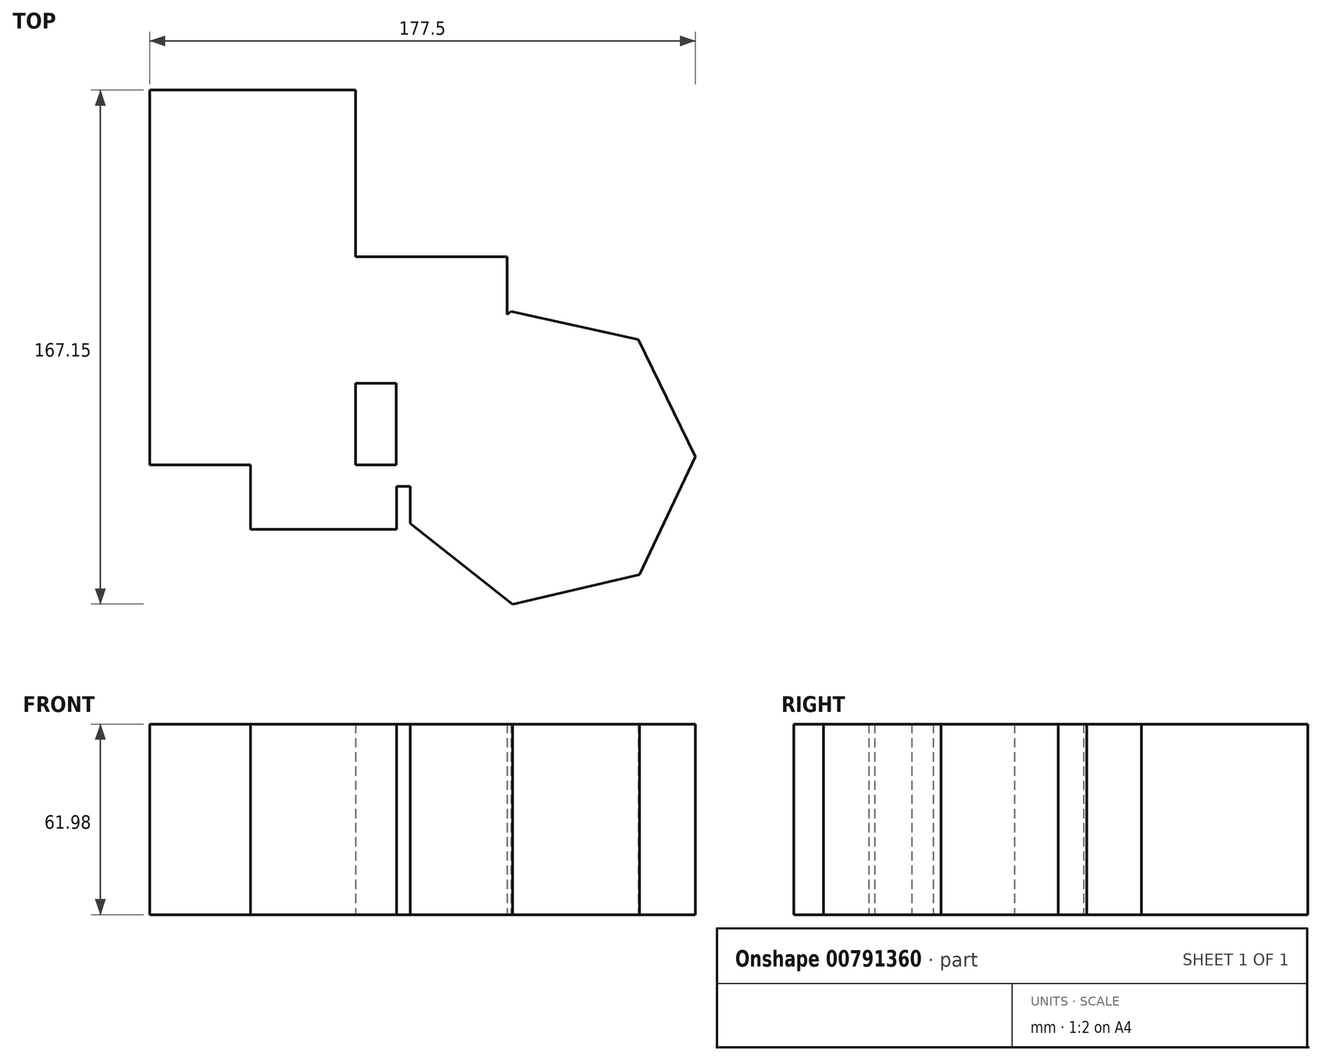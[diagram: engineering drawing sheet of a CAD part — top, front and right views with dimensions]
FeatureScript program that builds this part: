
annotation { "Feature Type Name" : "Feature", "Feature Type Description" : "" }
export const myFeature = defineFeature(function(context is Context, id is Id, definition is map)
    precondition{}
    {
        {
            var Q0;
            Q0=qCreatedBy(makeId("Top.planeOp"),FACE);
            var sketch = newSketch(context, id + "F0", { "sketchPlane" : qUnion([Q0])});
            skCircle(sketch, "E0.cCircle", {"center": v(-59.62, 9.79) * mm, "radius": 23.73 * mm, "construction": true});
            skLineSegment(sketch, "E0.0", {"start": v(-35.88, -13.95) * mm, "end": v(-83.35, -13.95) * mm});
            skLineSegment(sketch, "E0.1", {"start": v(-83.35, -13.95) * mm, "end": v(-83.35, 33.52) * mm});
            skLineSegment(sketch, "E0.2", {"start": v(-83.35, 33.52) * mm, "end": v(-35.88, 33.52) * mm});
            skLineSegment(sketch, "E0.3", {"start": v(-35.88, 33.52) * mm, "end": v(-35.88, -13.95) * mm});
            skPoint(sketch, "E0.0.midPoint", {"position": v(-59.62, -13.95) * mm});
            skCircle(sketch, "E1.cCircle", {"center": v(12.44, 9.4) * mm, "radius": 44 * mm, "construction": true});
            skLineSegment(sketch, "E1.0", {"start": v(43.08, -28.64) * mm, "end": v(1.81, -38.27) * mm});
            skLineSegment(sketch, "E1.1", {"start": v(1.81, -38.27) * mm, "end": v(-31.45, -12.01) * mm});
            skLineSegment(sketch, "E1.2", {"start": v(-31.45, -12.01) * mm, "end": v(-31.66, 30.37) * mm});
            skLineSegment(sketch, "E1.3", {"start": v(-31.66, 30.37) * mm, "end": v(1.34, 56.95) * mm});
            skLineSegment(sketch, "E1.4", {"start": v(1.34, 56.95) * mm, "end": v(42.7, 47.73) * mm});
            skLineSegment(sketch, "E1.5", {"start": v(42.7, 47.73) * mm, "end": v(61.28, 9.64) * mm});
            skLineSegment(sketch, "E1.6", {"start": v(61.28, 9.64) * mm, "end": v(43.08, -28.64) * mm});
            skPoint(sketch, "E1.0.midPoint", {"position": v(22.45, -33.46) * mm});
            skLineSegment(sketch, "E2.bottom", {"start": v(0, 0) * mm, "end": v(-49.22, 0) * mm});
            skLineSegment(sketch, "E2.top", {"start": v(0, 74.73) * mm, "end": v(-49.22, 74.73) * mm});
            skLineSegment(sketch, "E2.left", {"start": v(0, 0) * mm, "end": v(0, 74.73) * mm});
            skLineSegment(sketch, "E2.right", {"start": v(-49.22, 0) * mm, "end": v(-49.22, 74.73) * mm});
            skLineSegment(sketch, "E3.bottom", {"start": v(-49.22, 74.73) * mm, "end": v(-116.22, 74.73) * mm});
            skLineSegment(sketch, "E3.top", {"start": v(-49.22, 128.88) * mm, "end": v(-116.22, 128.88) * mm});
            skLineSegment(sketch, "E3.left", {"start": v(-49.22, 74.73) * mm, "end": v(-49.22, 128.88) * mm});
            skLineSegment(sketch, "E3.right", {"start": v(-116.22, 74.73) * mm, "end": v(-116.22, 128.88) * mm});
            skLineSegment(sketch, "E4.bottom", {"start": v(-116.22, 74.73) * mm, "end": v(-36.04, 74.73) * mm});
            skLineSegment(sketch, "E4.top", {"start": v(-116.22, 7.05) * mm, "end": v(-36.04, 7.05) * mm});
            skLineSegment(sketch, "E4.left", {"start": v(-116.22, 74.73) * mm, "end": v(-116.22, 7.05) * mm});
            skLineSegment(sketch, "E4.right", {"start": v(-36.04, 74.73) * mm, "end": v(-36.04, 7.05) * mm});
            skSolve(sketch);
        }
        {
            var Q0;
            {var subQ0=sQuery(id+"F0.wireOp",EDGE,"E2.bottom");var subQ1=sQuery(id+"F0.wireOp",EDGE,"E0.3");var subQ3=sQuery(id+"F0.wireOp",EDGE,"E2.right");var subQ6=sQuery(id+"F0.wireOp",EDGE,"E0.0");var subQ7=sQuery(id+"F0.wireOp",EDGE,"E0.1");var subQ8=sQuery(id+"F0.wireOp",EDGE,"E4.top");var subQ9=makeQuery(id+"F0.imprint","INTERSECT",VERTEX,{"derivedFrom":[subQ7,subQ8]});var subQ14=sQuery(id+"F0.wireOp",EDGE,"E1.2");var subQ21=sQuery(id+"F0.wireOp",EDGE,"E0.2");var subQ22=makeQuery(id+"F0.imprint","INTERSECT",VERTEX,{"derivedFrom":[subQ21,subQ1]});var subQ24=makeQuery(id+"F0.imprint","INTERSECT",VERTEX,{"derivedFrom":[subQ14,subQ0]});var subQ25=makeQuery(id+"F0.imprint","IMPRINT",EDGE,{"disambiguationData":[TD([[subQ24,-1.0]])],"derivedFrom":subQ14});var subQ28=makeQuery(id+"F0.imprint","IMPRINT",EDGE,{"disambiguationData":[TD([[subQ22,1.0]])],"derivedFrom":subQ21});var subQ32=makeQuery(id+"F0.imprint","IMPRINT",EDGE,{"disambiguationData":[TD([[subQ9,-1.0]])],"derivedFrom":subQ7});var subQ33=makeQuery(id+"F0.imprint","INTERSECT",VERTEX,{"derivedFrom":[subQ21,subQ3]});var subQ35=sQuery(id+"F0.wireOp",EDGE,"E3.bottom");var subQ36=makeQuery(id+"F0.imprint","IMPRINT",EDGE,{"derivedFrom":subQ35});Q0=qUnion([makeQuery(id+"F0.imprint","IMPRINT",FACE,{"disambiguationData":[TD([[subQ28,-1.0]])]}),makeQuery(id+"F0.imprint","IMPRINT",FACE,{"disambiguationData":[TD([[subQ25,-1.0]])]}),makeQuery(id+"F0.imprint","IMPRINT",FACE,{"disambiguationData":[TD([[makeQuery(id+"F0.imprint","IMPRINT",EDGE,{"disambiguationData":[TD([[subQ33,-1.0]])],"derivedFrom":subQ21}),1.0]])]}),makeQuery(id+"F0.imprint","IMPRINT",FACE,{"disambiguationData":[TD([[makeQuery(id+"F0.imprint","IMPRINT",EDGE,{"derivedFrom":sQuery(id+"F0.wireOp",EDGE,"E1.0")}),-1.0]])]}),makeQuery(id+"F0.imprint","IMPRINT",FACE,{"disambiguationData":[TD([[subQ36,1.0]])]}),makeQuery(id+"F0.imprint","IMPRINT",FACE,{"disambiguationData":[TD([[subQ36,-1.0]])]}),makeQuery(id+"F0.imprint","IMPRINT",FACE,{"disambiguationData":[TD([[subQ32,-1.0]])]}),makeQuery(id+"F0.imprint","IMPRINT",FACE,{"disambiguationData":[TD([[subQ28,1.0]])]}),makeQuery(id+"F0.imprint","IMPRINT",FACE,{"disambiguationData":[TD([[makeQuery(id+"F0.imprint","IMPRINT",EDGE,{"derivedFrom":subQ6}),-1.0]])]})]);}
            extrude(context, id + "F1", {"entities" : qUnion([Q0]), "depth" : 61.98 * mm, "offsetDistance" : 25.4 * mm});
        }
    });
